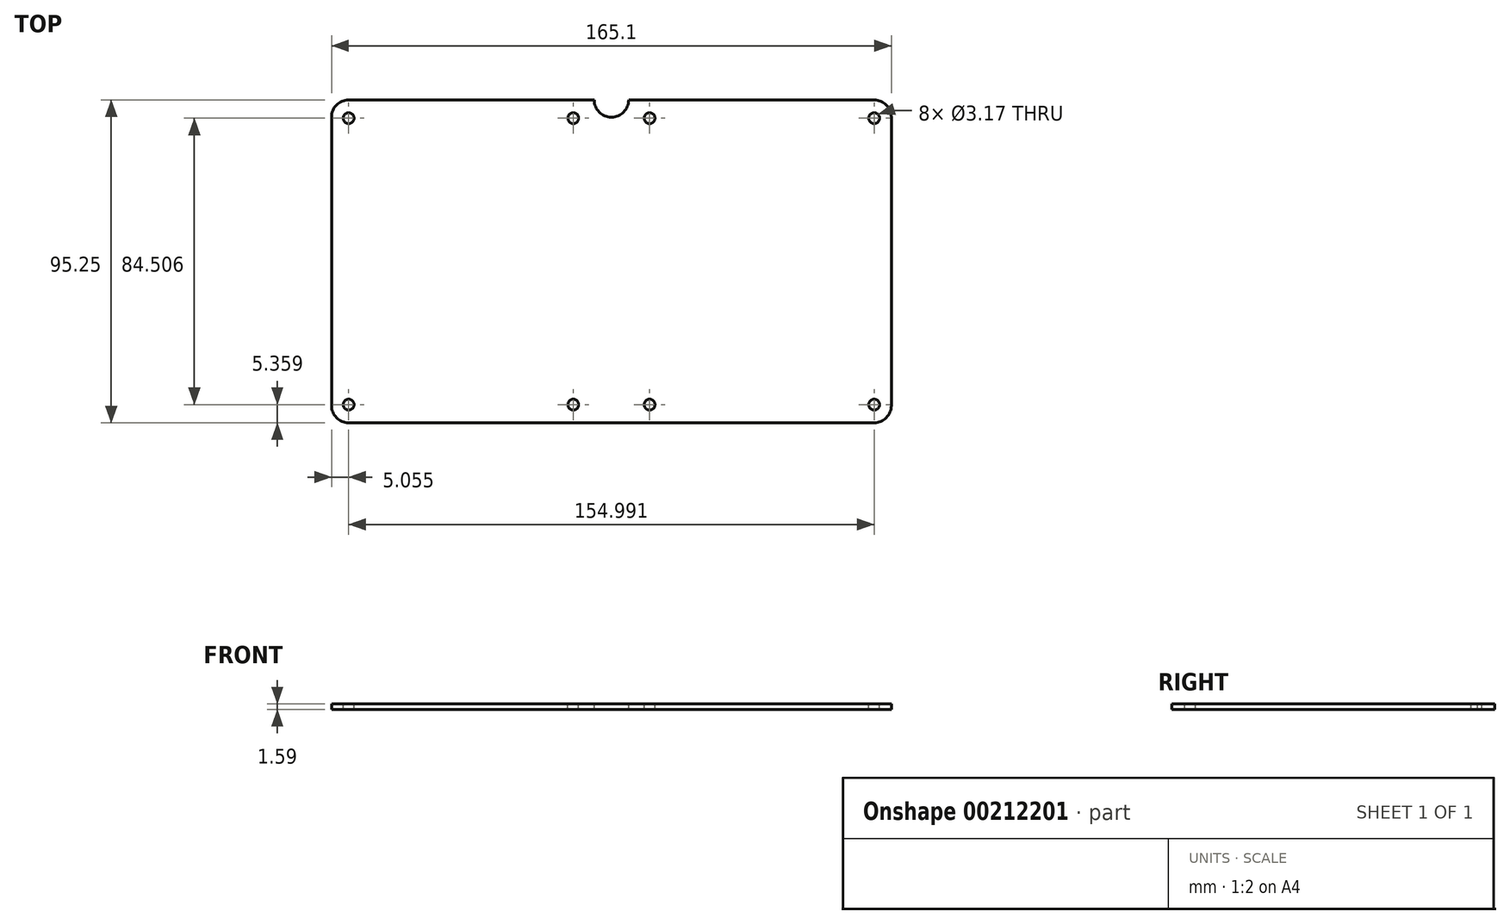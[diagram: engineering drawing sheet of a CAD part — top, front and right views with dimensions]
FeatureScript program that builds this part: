
annotation { "Feature Type Name" : "Feature", "Feature Type Description" : "" }
export const myFeature = defineFeature(function(context is Context, id is Id, definition is map)
    precondition{}
    {
        {
            var Q0;
            Q0=qCreatedBy(makeId("Top.planeOp"),FACE);
            var sketch = newSketch(context, id + "F0", { "sketchPlane" : qUnion([Q0])});
            skLineSegment(sketch, "E0.bottom", {"start": v(5.08, 0) * mm, "end": v(160.02, 0) * mm});
            skLineSegment(sketch, "E0.top", {"start": v(5.08, 95.25) * mm, "end": v(160.02, 95.25) * mm});
            skLineSegment(sketch, "E0.left", {"start": v(0, 5.08) * mm, "end": v(0, 90.17) * mm});
            skLineSegment(sketch, "E0.right", {"start": v(165.1, 5.08) * mm, "end": v(165.1, 90.17) * mm});
            skPoint(sketch, "E1.visualSharp", {"position": v(0, 95.25) * mm});
            skArc(sketch, "E1.filletArc", {"start": v(5.08, 95.25) * mm, "mid": v(1.49, 93.76) * mm, "end": v(0, 90.17) * mm});
            skPoint(sketch, "E2.visualSharp", {"position": v(165.1, 95.25) * mm});
            skArc(sketch, "E2.filletArc", {"start": v(165.1, 90.17) * mm, "mid": v(163.61, 93.76) * mm, "end": v(160.02, 95.25) * mm});
            skPoint(sketch, "E3.visualSharp", {"position": v(165.1, 0) * mm});
            skArc(sketch, "E3.filletArc", {"start": v(160.02, 0) * mm, "mid": v(163.61, 1.49) * mm, "end": v(165.1, 5.08) * mm});
            skPoint(sketch, "E4.visualSharp", {"position": v(0, 0) * mm});
            skArc(sketch, "E4.filletArc", {"start": v(0, 5.08) * mm, "mid": v(1.49, 1.49) * mm, "end": v(5.08, 0) * mm});
            skPoint(sketch, "E5", {"position": v(5.05, 5.36) * mm});
            skPoint(sketch, "E6", {"position": v(71.3, 5.36) * mm});
            skPoint(sketch, "E7", {"position": v(93.8, 5.36) * mm});
            skPoint(sketch, "E8", {"position": v(160.05, 5.36) * mm});
            skPoint(sketch, "E9", {"position": v(160.05, 89.87) * mm});
            skPoint(sketch, "E10", {"position": v(93.8, 89.87) * mm});
            skPoint(sketch, "E11", {"position": v(71.3, 89.87) * mm});
            skPoint(sketch, "E12", {"position": v(5.05, 89.87) * mm});
            skArc(sketch, "E13", {"start": v(77.47, 95.25) * mm, "mid": v(82.55, 90.17) * mm, "end": v(87.63, 95.25) * mm});
            skSolve(sketch);
        }
        {
            var Q0;
            Q0=makeQuery(id+"F0.imprint","IMPRINT",FACE,{"disambiguationData":[TD([[makeQuery(id+"F0.imprint","IMPRINT",EDGE,{"derivedFrom":sQuery(id+"F0.wireOp",EDGE,"E0.bottom")}),1.0]])]});
            extrude(context, id + "F1", {"entities" : qUnion([Q0]), "oppositeDirection" : true, "depth" : 1.59 * mm});
        }
        {
            var Q0;
            Q0=sQuery(id+"F0.wireOp",VERTEX,"E5");
            var Q1;
            Q1=sQuery(id+"F0.wireOp",VERTEX,"E6");
            var Q2;
            Q2=sQuery(id+"F0.wireOp",VERTEX,"E7");
            var Q3;
            Q3=sQuery(id+"F0.wireOp",VERTEX,"E8");
            var Q4;
            Q4=sQuery(id+"F0.wireOp",VERTEX,"E9");
            var Q5;
            Q5=sQuery(id+"F0.wireOp",VERTEX,"E10");
            var Q6;
            Q6=sQuery(id+"F0.wireOp",VERTEX,"E11");
            var Q7;
            Q7=sQuery(id+"F0.wireOp",VERTEX,"E12");
            var Q8;
            Q8=makeQuery(id+"F1.opExtrude","SWEPT_BODY",BODY,{"disambiguationData":[OSD([sQuery(id+"F0.wireOp",EDGE,"E0.bottom"),sQuery(id+"F0.wireOp",EDGE,"E0.top"),sQuery(id+"F0.wireOp",EDGE,"E0.left"),sQuery(id+"F0.wireOp",EDGE,"E0.right"),sQuery(id+"F0.wireOp",EDGE,"E1.filletArc"),sQuery(id+"F0.wireOp",EDGE,"E2.filletArc"),sQuery(id+"F0.wireOp",EDGE,"E3.filletArc"),sQuery(id+"F0.wireOp",EDGE,"E4.filletArc")])]});
            hole(context, id + "F2", {"style" : HoleStyle.SIMPLE, "endStyle" : HoleEndStyle.THROUGH, "holeDiameter" : 3.17 * mm, "locations" : qUnion([Q0, Q1, Q2, Q3, Q4, Q5, Q6, Q7]), "scope" : qUnion([Q8]), "isTappedThrough" : true});
        }
    });
